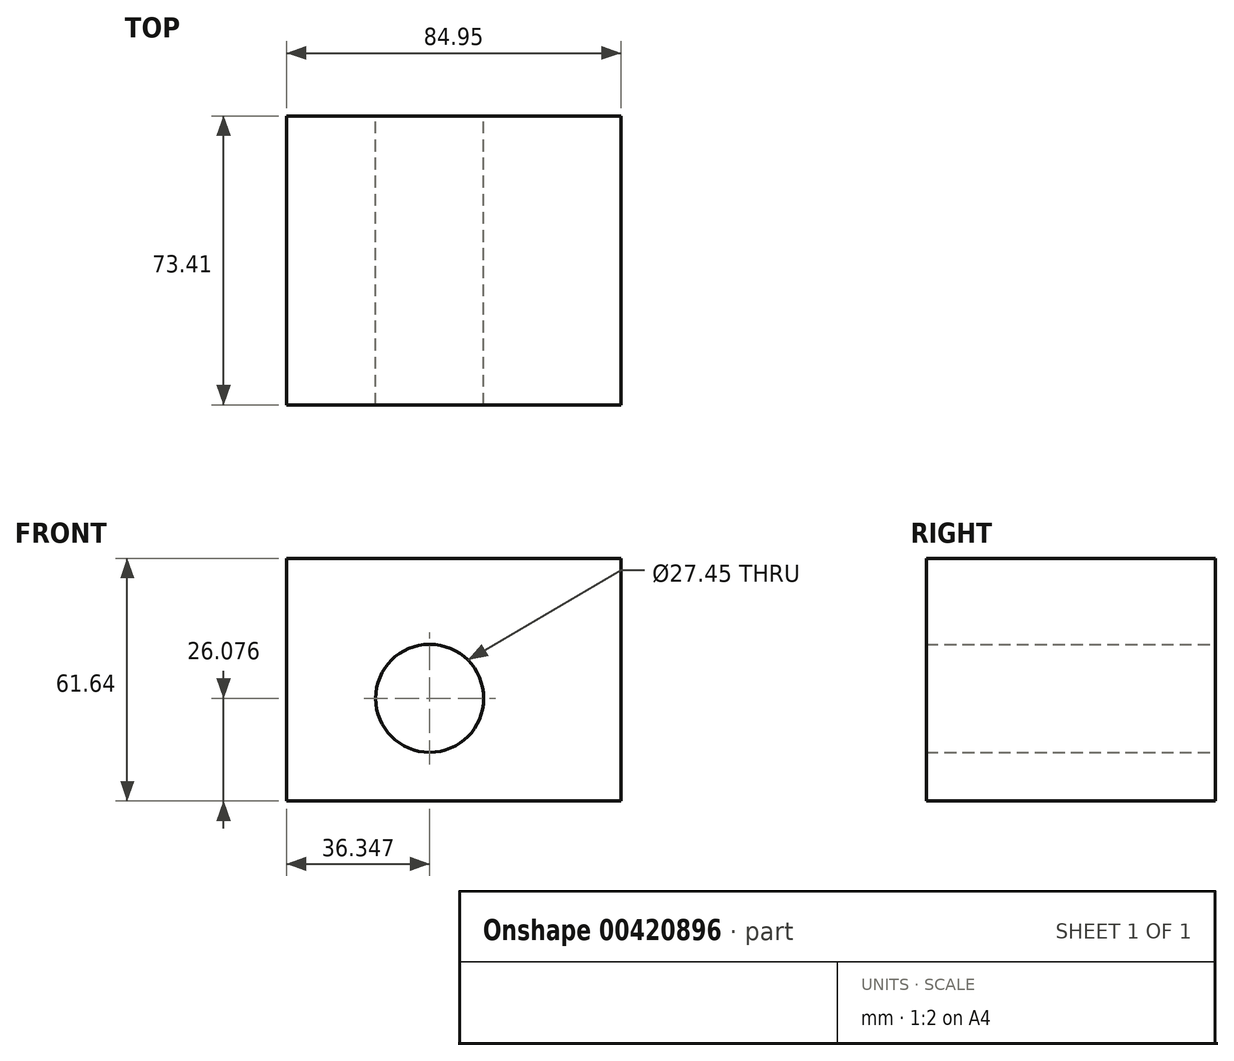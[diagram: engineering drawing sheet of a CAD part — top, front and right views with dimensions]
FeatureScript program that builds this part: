
annotation { "Feature Type Name" : "Feature", "Feature Type Description" : "" }
export const myFeature = defineFeature(function(context is Context, id is Id, definition is map)
    precondition{}
    {
        {
            var Q0;
            Q0=qCreatedBy(makeId("Front.planeOp"),FACE);
            var sketch = newSketch(context, id + "F0", { "sketchPlane" : qUnion([Q0])});
            skLineSegment(sketch, "E0", {"start": v(-48.2, 28.65) * mm, "end": v(-48.2, -33) * mm});
            skLineSegment(sketch, "E1", {"start": v(-48.2, -33) * mm, "end": v(36.75, -33) * mm});
            skLineSegment(sketch, "E2", {"start": v(36.75, -33) * mm, "end": v(36.75, 28.65) * mm});
            skLineSegment(sketch, "E3", {"start": v(36.75, 28.65) * mm, "end": v(-48.2, 28.65) * mm});
            skCircle(sketch, "E4", {"center": v(-11.85, -6.91) * mm, "radius": 13.72 * mm});
            skSolve(sketch);
        }
        {
            var Q0;
            Q0=makeQuery(id+"F0.imprint","IMPRINT",FACE,{"disambiguationData":[TD([[makeQuery(id+"F0.imprint","IMPRINT",EDGE,{"derivedFrom":sQuery(id+"F0.wireOp",EDGE,"E0")}),1.0]])]});
            extrude(context, id + "F1", {"entities" : qUnion([Q0]), "depth" : 73.4 * mm});
        }
    });
